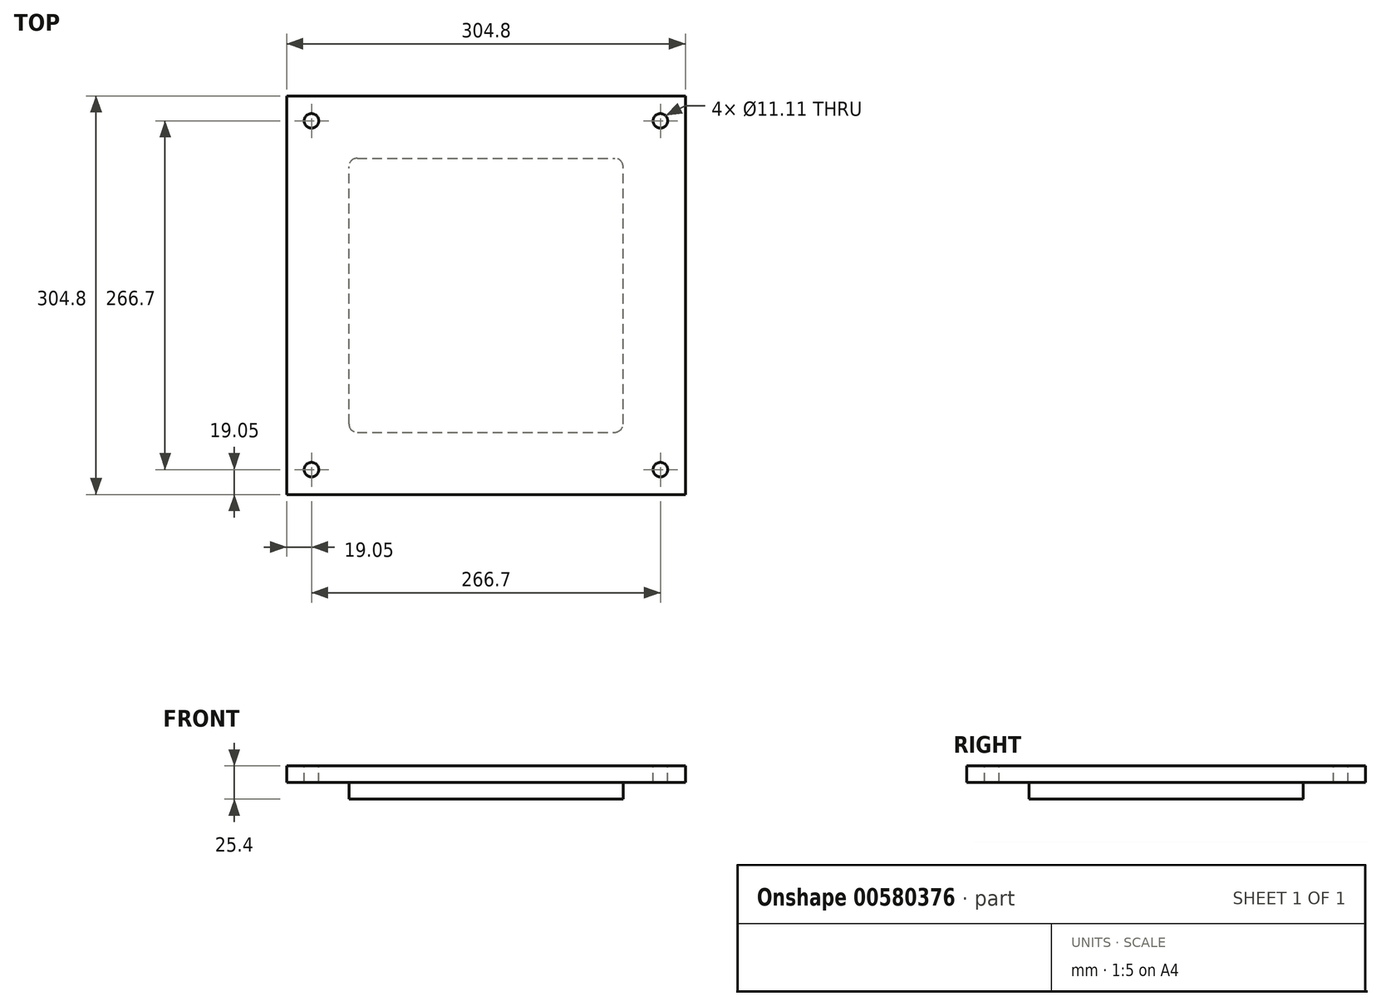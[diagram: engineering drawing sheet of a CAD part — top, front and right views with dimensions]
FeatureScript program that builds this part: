
annotation { "Feature Type Name" : "Feature", "Feature Type Description" : "" }
export const myFeature = defineFeature(function(context is Context, id is Id, definition is map)
    precondition{}
    {
        {
            var Q0;
            Q0=qCreatedBy(makeId("Top.planeOp"),FACE);
            var sketch = newSketch(context, id + "F0", { "sketchPlane" : qUnion([Q0])});
            skLineSegment(sketch, "E0.bottom", {"start": v(-152.4, 152.4) * mm, "end": v(152.4, 152.4) * mm});
            skLineSegment(sketch, "E0.top", {"start": v(-152.4, -152.4) * mm, "end": v(152.4, -152.4) * mm});
            skLineSegment(sketch, "E0.left", {"start": v(-152.4, 152.4) * mm, "end": v(-152.4, -152.4) * mm});
            skLineSegment(sketch, "E0.right", {"start": v(152.4, 152.4) * mm, "end": v(152.4, -152.4) * mm});
            skSolve(sketch);
        }
        {
            var Q0;
            Q0 = qSketchRegion(id + "F0", true);
            extrude(context, id + "F1", {"entities" : qUnion([Q0]), "depth" : 12.7 * mm, "offsetDistance" : 25.4 * mm});
        }
        {
            var Q0;
            Q0=makeQuery(id+"F1.opExtrude","CAP_FACE",FACE,{"disambiguationData":[OSD([sQuery(id+"F0.wireOp",EDGE,"E0.bottom"),sQuery(id+"F0.wireOp",EDGE,"E0.top"),sQuery(id+"F0.wireOp",EDGE,"E0.left"),sQuery(id+"F0.wireOp",EDGE,"E0.right")])],"isStart":true});
            var sketch = newSketch(context, id + "F2", { "sketchPlane" : qUnion([Q0])});
            skLineSegment(sketch, "E1.bottom", {"start": v(-98.43, 104.78) * mm, "end": v(98.43, 104.78) * mm});
            skLineSegment(sketch, "E1.top", {"start": v(-98.43, -104.78) * mm, "end": v(98.43, -104.78) * mm});
            skLineSegment(sketch, "E1.left", {"start": v(-104.78, 98.43) * mm, "end": v(-104.78, -98.43) * mm});
            skLineSegment(sketch, "E1.right", {"start": v(104.78, 98.43) * mm, "end": v(104.78, -98.43) * mm});
            skPoint(sketch, "E2.visualSharp", {"position": v(-104.78, -104.78) * mm});
            skArc(sketch, "E2.filletArc", {"start": v(-104.78, -98.43) * mm, "mid": v(-102.92, -102.92) * mm, "end": v(-98.43, -104.78) * mm});
            skPoint(sketch, "E3.visualSharp", {"position": v(104.78, -104.78) * mm});
            skArc(sketch, "E3.filletArc", {"start": v(98.43, -104.78) * mm, "mid": v(102.92, -102.92) * mm, "end": v(104.78, -98.43) * mm});
            skPoint(sketch, "E4.visualSharp", {"position": v(104.78, 104.78) * mm});
            skArc(sketch, "E4.filletArc", {"start": v(104.78, 98.43) * mm, "mid": v(102.92, 102.92) * mm, "end": v(98.43, 104.78) * mm});
            skPoint(sketch, "E5.visualSharp", {"position": v(-104.78, 104.78) * mm});
            skArc(sketch, "E5.filletArc", {"start": v(-98.43, 104.78) * mm, "mid": v(-102.92, 102.92) * mm, "end": v(-104.78, 98.43) * mm});
            skSolve(sketch);
        }
        {
            var Q0;
            Q0 = qSketchRegion(id + "F2", true);
            extrude(context, id + "F3", {"entities" : qUnion([Q0]), "operationType" : NewBodyOperationType.ADD, "depth" : 12.7 * mm, "offsetDistance" : 25.4 * mm});
        }
        {
            var Q0;
            Q0=makeQuery(id+"F1.opExtrude","CAP_FACE",FACE,{"disambiguationData":[OSD([sQuery(id+"F0.wireOp",EDGE,"E0.bottom"),sQuery(id+"F0.wireOp",EDGE,"E0.top"),sQuery(id+"F0.wireOp",EDGE,"E0.left"),sQuery(id+"F0.wireOp",EDGE,"E0.right")])],"isStart":false});
            var sketch = newSketch(context, id + "F4", { "sketchPlane" : qUnion([Q0])});
            skPoint(sketch, "E6", {"position": v(-133.35, 133.35) * mm});
            skPoint(sketch, "E7", {"position": v(133.35, 133.35) * mm});
            skPoint(sketch, "E8", {"position": v(133.35, -133.35) * mm});
            skPoint(sketch, "E9", {"position": v(-133.35, -133.35) * mm});
            skSolve(sketch);
        }
        {
            var Q0;
            Q0=sQuery(id+"F4.wireOp",VERTEX,"E6");
            var Q1;
            Q1=sQuery(id+"F4.wireOp",VERTEX,"E7");
            var Q2;
            Q2=sQuery(id+"F4.wireOp",VERTEX,"E8");
            var Q3;
            Q3=sQuery(id+"F4.wireOp",VERTEX,"E9");
            var Q4;
            Q4=makeQuery(id+"F1.opExtrude","SWEPT_BODY",BODY,{"disambiguationData":[OSD([sQuery(id+"F0.wireOp",EDGE,"E0.bottom"),sQuery(id+"F0.wireOp",EDGE,"E0.top"),sQuery(id+"F0.wireOp",EDGE,"E0.left"),sQuery(id+"F0.wireOp",EDGE,"E0.right")])]});
            hole(context, id + "F5", {"style" : HoleStyle.SIMPLE, "endStyle" : HoleEndStyle.THROUGH, "holeDiameter" : 11.1 * mm, "majorDiameter" : 6.35 * mm, "isTappedThrough" : true, "tappedDepth" : 12.7 * mm, "tapClearance" : 3, "locations" : qUnion([Q0, Q1, Q2, Q3]), "scope" : qUnion([Q4])});
        }
    });
